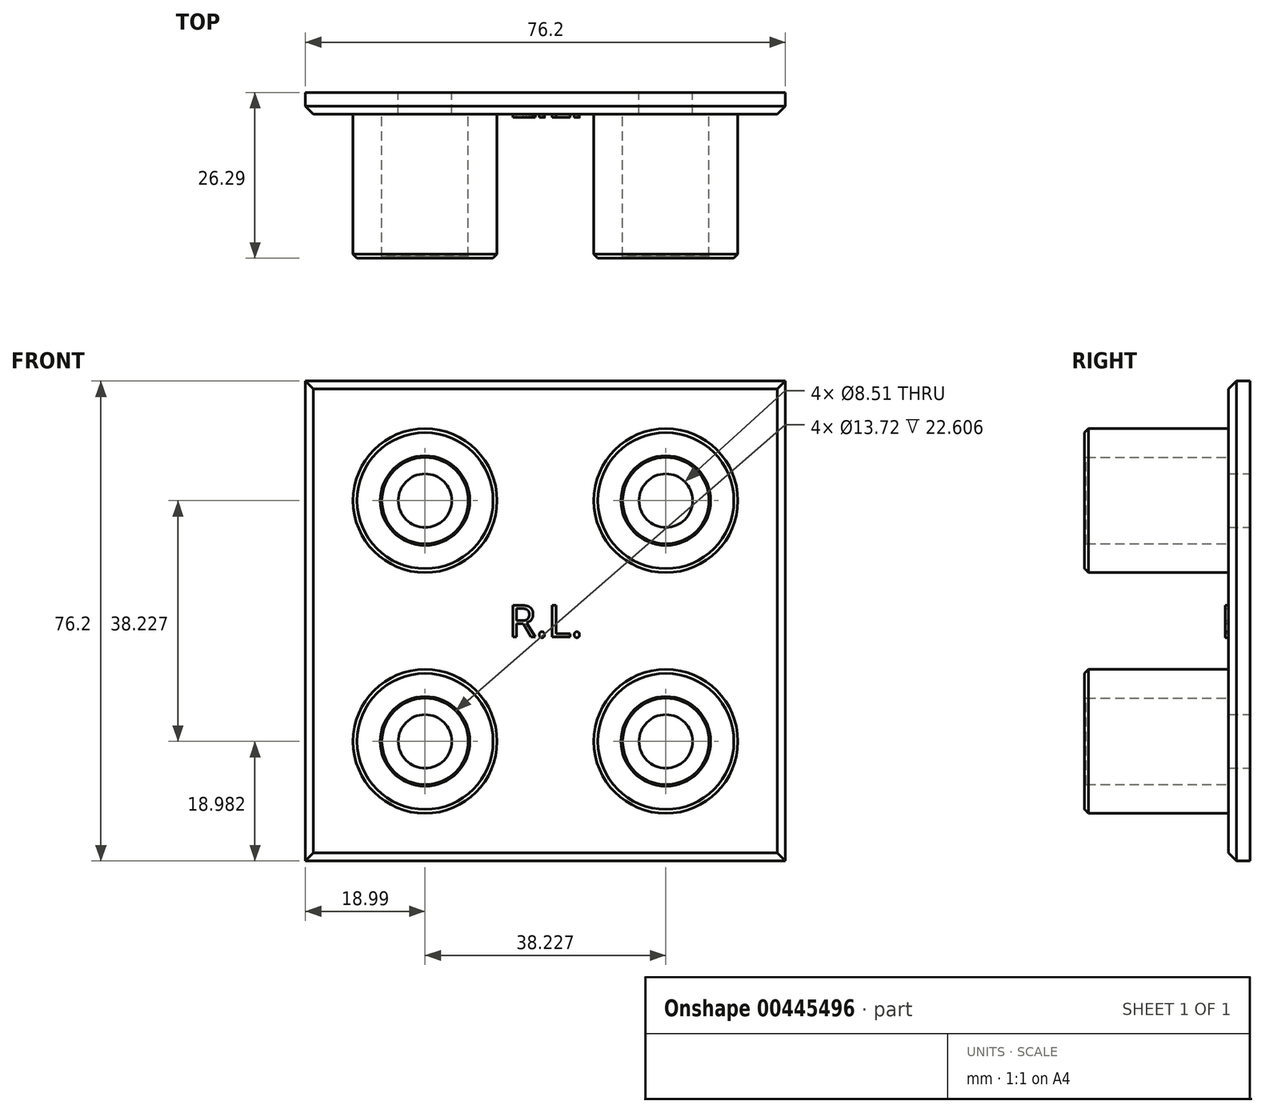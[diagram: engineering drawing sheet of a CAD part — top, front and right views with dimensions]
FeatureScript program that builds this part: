
annotation { "Feature Type Name" : "Feature", "Feature Type Description" : "" }
export const myFeature = defineFeature(function(context is Context, id is Id, definition is map)
    precondition{}
    {
        {
            var Q0;
            Q0=qCreatedBy(makeId("Front.planeOp"),FACE);
            var sketch = newSketch(context, id + "F0", { "sketchPlane" : qUnion([Q0])});
            skLineSegment(sketch, "E0.bottom", {"start": v(27.65, -18.95) * mm, "end": v(-48.55, -18.95) * mm});
            skLineSegment(sketch, "E0.top", {"start": v(27.65, 57.25) * mm, "end": v(-48.55, 57.25) * mm});
            skLineSegment(sketch, "E0.left", {"start": v(27.65, -18.95) * mm, "end": v(27.65, 57.25) * mm});
            skLineSegment(sketch, "E0.right", {"start": v(-48.55, -18.95) * mm, "end": v(-48.55, 57.25) * mm});
            skPoint(sketch, "E0.middle", {"position": v(-10.45, 19.15) * mm});
            skSolve(sketch);
        }
        {
            var Q0;
            Q0=makeQuery(id+"F0.imprint","IMPRINT",FACE,{"disambiguationData":[TD([[makeQuery(id+"F0.imprint","IMPRINT",EDGE,{"derivedFrom":sQuery(id+"F0.wireOp",EDGE,"E0.bottom")}),-1.0]])]});
            var sketch = newSketch(context, id + "F1", { "sketchPlane" : qUnion([Q0])});
            skCircle(sketch, "E1", {"center": v(-29.56, 38.26) * mm, "radius": 4.25 * mm});
            skCircle(sketch, "E2", {"center": v(8.67, 38.26) * mm, "radius": 4.25 * mm});
            skCircle(sketch, "E3", {"center": v(-29.56, 0.03) * mm, "radius": 4.25 * mm});
            skCircle(sketch, "E4", {"center": v(8.67, 0.03) * mm, "radius": 4.25 * mm});
            skSolve(sketch);
        }
        {
            var Q0;
            Q0=makeQuery(id+"F0.imprint","IMPRINT",FACE,{"disambiguationData":[TD([[makeQuery(id+"F0.imprint","IMPRINT",EDGE,{"derivedFrom":sQuery(id+"F0.wireOp",EDGE,"E0.bottom")}),-1.0]])]});
            extrude(context, id + "F2", {"entities" : qUnion([Q0]), "depth" : 3.43 * mm});
        }
        {
            var Q0;
            Q0 = qSketchRegion(id + "F1", true);
            extrude(context, id + "F3", {"entities" : qUnion([Q0]), "operationType" : NewBodyOperationType.REMOVE, "oppositeDirection" : true, "depth" : -3.56 * mm});
        }
        {
            var Q0;
            Q0=makeQuery(id+"F2.opExtrude","CAP_FACE",FACE,{"disambiguationData":[OSD([sQuery(id+"F0.wireOp",EDGE,"E0.bottom"),sQuery(id+"F0.wireOp",EDGE,"E0.top"),sQuery(id+"F0.wireOp",EDGE,"E0.left"),sQuery(id+"F0.wireOp",EDGE,"E0.right")])],"isStart":false});
            var sketch = newSketch(context, id + "F4", { "sketchPlane" : qUnion([Q0])});
            skCircle(sketch, "E5", {"center": v(-29.56, 38.26) * mm, "radius": 6.86 * mm});
            skCircle(sketch, "E6", {"center": v(-29.56, 0.03) * mm, "radius": 6.86 * mm});
            skCircle(sketch, "E7", {"center": v(8.67, 38.26) * mm, "radius": 6.86 * mm});
            skCircle(sketch, "E8", {"center": v(8.67, 0.03) * mm, "radius": 6.86 * mm});
            skCircle(sketch, "E9", {"center": v(-29.56, 38.26) * mm, "radius": 11.43 * mm});
            skCircle(sketch, "E10", {"center": v(8.67, 38.26) * mm, "radius": 11.43 * mm});
            skCircle(sketch, "E11", {"center": v(-29.56, 0.03) * mm, "radius": 11.43 * mm});
            skCircle(sketch, "E12", {"center": v(8.67, 0.03) * mm, "radius": 11.43 * mm});
            skSolve(sketch);
        }
        {
            var Q0;
            Q0 = qSketchRegion(id + "F4", true);
            extrude(context, id + "F5", {"entities" : qUnion([Q0]), "operationType" : NewBodyOperationType.ADD, "depth" : 22.86 * mm});
        }
        {
            var Q0;
            Q0=makeQuery(id+"F2.opExtrude","CAP_EDGE",EDGE,{"disambiguationData":[OSD([sQuery(id+"F0.wireOp",EDGE,"E0.top")])],"isStart":false});
            var Q1;
            Q1=makeQuery(id+"F2.opExtrude","CAP_EDGE",EDGE,{"disambiguationData":[OSD([sQuery(id+"F0.wireOp",EDGE,"E0.left")])],"isStart":false});
            var Q2;
            Q2=makeQuery(id+"F2.opExtrude","CAP_EDGE",EDGE,{"disambiguationData":[OSD([sQuery(id+"F0.wireOp",EDGE,"E0.bottom")])],"isStart":false});
            var Q3;
            Q3=makeQuery(id+"F2.opExtrude","CAP_EDGE",EDGE,{"disambiguationData":[OSD([sQuery(id+"F0.wireOp",EDGE,"E0.right")])],"isStart":false});
            chamfer(context, id + "F6", {"entities" : qUnion([Q0, Q1, Q2, Q3]), "width" : 1.27 * mm, "tangentPropagation" : true});
        }
        {
            var Q0;
            Q0=makeQuery(id+"F5.opExtrude","CAP_EDGE",EDGE,{"disambiguationData":[OSD([sQuery(id+"F4.wireOp",EDGE,"E9")])],"isStart":false});
            var Q1;
            Q1=makeQuery(id+"F5.opExtrude","CAP_EDGE",EDGE,{"disambiguationData":[OSD([sQuery(id+"F4.wireOp",EDGE,"E10")])],"isStart":false});
            var Q2;
            Q2=makeQuery(id+"F5.opExtrude","CAP_EDGE",EDGE,{"disambiguationData":[OSD([sQuery(id+"F4.wireOp",EDGE,"E12")])],"isStart":false});
            var Q3;
            Q3=makeQuery(id+"F5.opExtrude","CAP_EDGE",EDGE,{"disambiguationData":[OSD([sQuery(id+"F4.wireOp",EDGE,"E11")])],"isStart":false});
            chamfer(context, id + "F7", {"entities" : qUnion([Q0, Q1, Q2, Q3]), "width" : 0.64 * mm, "tangentPropagation" : true});
        }
        {
            var Q0;
            Q0=makeQuery(id+"F5.opExtrude","CAP_EDGE",EDGE,{"disambiguationData":[OSD([sQuery(id+"F4.wireOp",EDGE,"E5")])],"isStart":false});
            var Q1;
            Q1=makeQuery(id+"F5.opExtrude","CAP_EDGE",EDGE,{"disambiguationData":[OSD([sQuery(id+"F4.wireOp",EDGE,"E7")])],"isStart":false});
            var Q2;
            Q2=makeQuery(id+"F5.opExtrude","CAP_EDGE",EDGE,{"disambiguationData":[OSD([sQuery(id+"F4.wireOp",EDGE,"E8")])],"isStart":false});
            var Q3;
            Q3=makeQuery(id+"F5.opExtrude","CAP_EDGE",EDGE,{"disambiguationData":[OSD([sQuery(id+"F4.wireOp",EDGE,"E6")])],"isStart":false});
            chamfer(context, id + "F8", {"entities" : qUnion([Q0, Q1, Q2, Q3]), "width" : 0.25 * mm, "tangentPropagation" : true});
        }
        {
            var Q0;
            {var subQ0=sQuery(id+"F0.wireOp",EDGE,"E0.left");var subQ1=sQuery(id+"F0.wireOp",EDGE,"E0.top");var subQ2=sQuery(id+"F0.wireOp",EDGE,"E0.right");var subQ3=sQuery(id+"F0.wireOp",EDGE,"E0.bottom");Q0=makeQuery(id+"F5.boolean.opBoolean","SPLIT",FACE,{"disambiguationData":[TD([makeQuery(id+"F2.opExtrude","SWEPT_FACE",FACE,{"disambiguationData":[OSD([subQ3])]})])],"derivedFrom":makeQuery(id+"F2.opExtrude","CAP_FACE",FACE,{"disambiguationData":[OSD([subQ3,subQ1,subQ0,subQ2])],"isStart":false})});}
            var sketch = newSketch(context, id + "F9", { "sketchPlane" : qUnion([Q0])});
            skText(sketch, "E13", { "text": "R.L.", "fontName": "OpenSans-Regular.ttf"});
            const initialGuessF9  = {"E13": [-0.0163, 0.0166, 1, 0, 0.00508]};
            skSetInitialGuess(sketch, initialGuessF9);
            skSolve(sketch);
        }
        {
            var Q0;
            Q0 = qSketchRegion(id + "F9", true);
            extrude(context, id + "F10", {"entities" : qUnion([Q0]), "operationType" : NewBodyOperationType.ADD, "depth" : 0.5 * mm});
        }
    });
